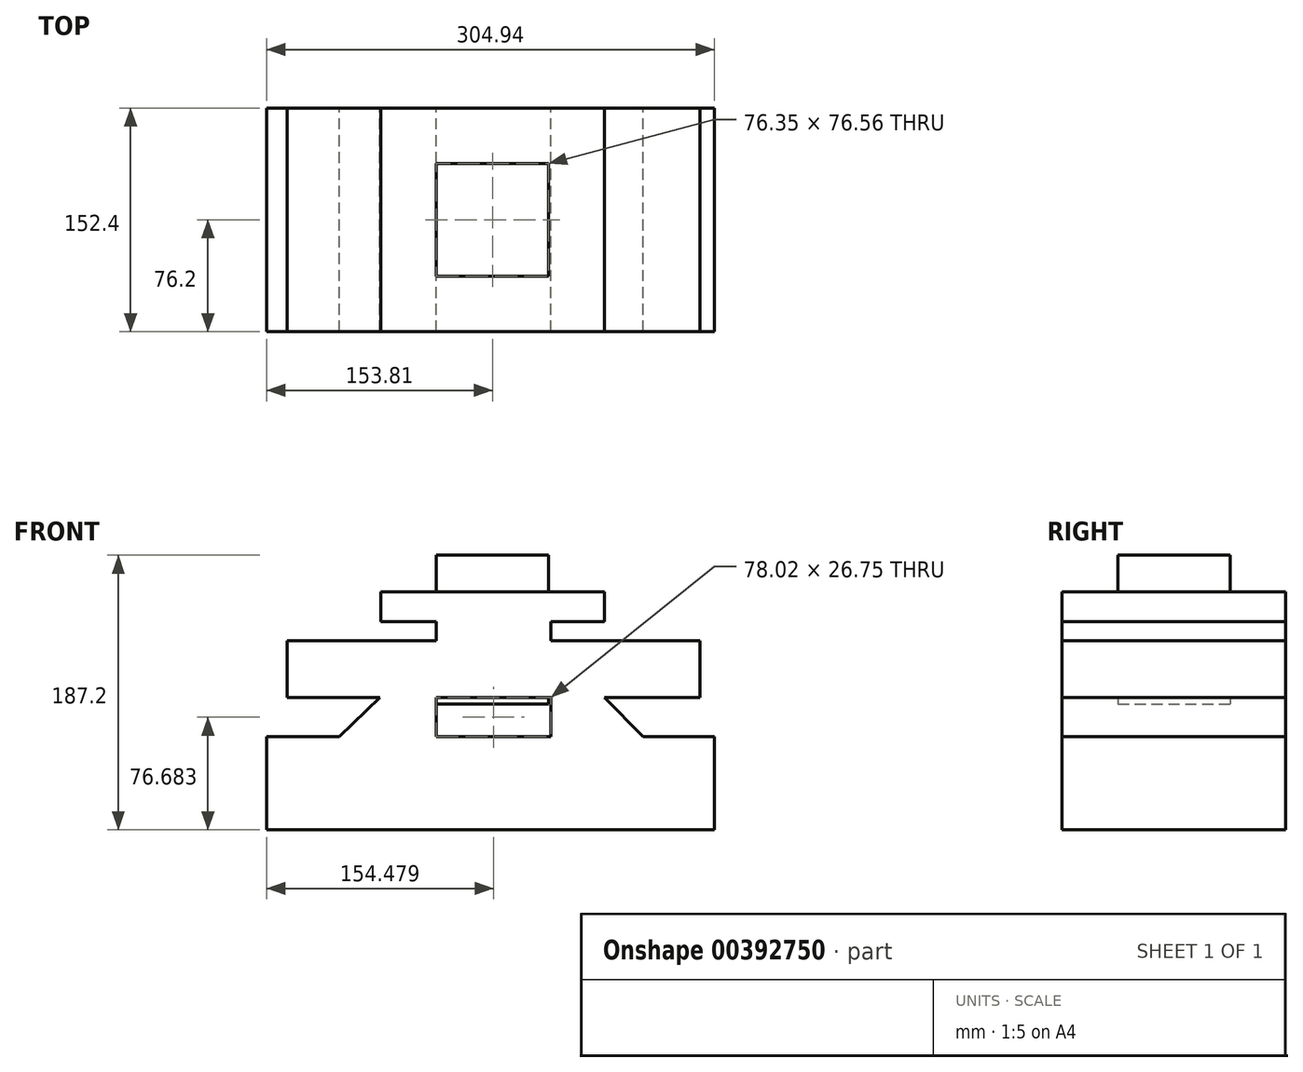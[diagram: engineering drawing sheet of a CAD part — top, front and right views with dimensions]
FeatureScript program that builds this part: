
annotation { "Feature Type Name" : "Feature", "Feature Type Description" : "" }
export const myFeature = defineFeature(function(context is Context, id is Id, definition is map)
    precondition{}
    {
        {
            var Q0;
            Q0=qCreatedBy(makeId("Front.planeOp"),FACE);
            var sketch = newSketch(context, id + "F0", { "sketchPlane" : qUnion([Q0])});
            skLineSegment(sketch, "E0", {"start": v(-153.8, -85.6) * mm, "end": v(151.13, -85.6) * mm});
            skLineSegment(sketch, "E1", {"start": v(151.13, -85.6) * mm, "end": v(151.13, -22.3) * mm});
            skLineSegment(sketch, "E2", {"start": v(-153.8, -85.6) * mm, "end": v(-153.8, -22.3) * mm});
            skLineSegment(sketch, "E3", {"start": v(-153.8, -22.3) * mm, "end": v(151.13, -22.3) * mm});
            skLineSegment(sketch, "E4", {"start": v(-38.34, -22.3) * mm, "end": v(-38.34, 4.46) * mm});
            skLineSegment(sketch, "E5", {"start": v(-38.34, 4.46) * mm, "end": v(39.68, 4.46) * mm});
            skLineSegment(sketch, "E6", {"start": v(39.68, 4.46) * mm, "end": v(39.68, -22.3) * mm});
            skLineSegment(sketch, "E7", {"start": v(-38.34, 4.46) * mm, "end": v(-139.99, 4.46) * mm});
            skLineSegment(sketch, "E8", {"start": v(39.68, 4.46) * mm, "end": v(141.33, 4.46) * mm});
            skLineSegment(sketch, "E9", {"start": v(-139.99, 4.46) * mm, "end": v(-139.99, 43.24) * mm});
            skLineSegment(sketch, "E10", {"start": v(-139.99, 43.24) * mm, "end": v(141.33, 43.24) * mm});
            skLineSegment(sketch, "E11", {"start": v(141.33, 43.24) * mm, "end": v(141.33, 4.46) * mm});
            skLineSegment(sketch, "E12", {"start": v(-76.68, 43.24) * mm, "end": v(-76.68, 4.46) * mm});
            skLineSegment(sketch, "E13", {"start": v(0, 4.46) * mm, "end": v(0, 43.24) * mm});
            skLineSegment(sketch, "E14", {"start": v(76.24, 43.24) * mm, "end": v(76.24, 4.46) * mm});
            skLineSegment(sketch, "E15", {"start": v(-38.34, 43.24) * mm, "end": v(-38.34, 56.17) * mm});
            skLineSegment(sketch, "E16", {"start": v(39.68, 56.17) * mm, "end": v(-38.34, 56.17) * mm});
            skLineSegment(sketch, "E17", {"start": v(39.68, 56.17) * mm, "end": v(39.68, 43.24) * mm});
            skLineSegment(sketch, "E18", {"start": v(-38.34, 56.17) * mm, "end": v(-76.24, 56.17) * mm});
            skLineSegment(sketch, "E19", {"start": v(-76.24, 56.17) * mm, "end": v(-76.24, 76.68) * mm});
            skLineSegment(sketch, "E20", {"start": v(-76.24, 76.68) * mm, "end": v(76.24, 76.68) * mm});
            skLineSegment(sketch, "E21", {"start": v(39.68, 56.17) * mm, "end": v(76.24, 56.17) * mm});
            skLineSegment(sketch, "E22", {"start": v(76.24, 56.17) * mm, "end": v(76.24, 76.68) * mm});
            skLineSegment(sketch, "E23", {"start": v(-76.68, 4.46) * mm, "end": v(-104.32, -22.3) * mm});
            skLineSegment(sketch, "E24", {"start": v(76.24, 4.46) * mm, "end": v(102.54, -22.3) * mm});
            skSolve(sketch);
        }
        {
            var Q0;
            Q0 = qSketchRegion(id + "F0", true);
            extrude(context, id + "F1", {"entities" : qUnion([Q0]), "endBound" : BoundingType.SYMMETRIC, "depth" : 152.4 * mm});
        }
        {
            var Q0;
            Q0=qCreatedBy(makeId("Top.planeOp"),FACE);
            var sketch = newSketch(context, id + "F2", { "sketchPlane" : qUnion([Q0])});
            skLineSegment(sketch, "E25.bottom", {"start": v(-38.18, -38.28) * mm, "end": v(38.18, -38.28) * mm});
            skLineSegment(sketch, "E25.top", {"start": v(-38.18, 38.28) * mm, "end": v(38.18, 38.28) * mm});
            skLineSegment(sketch, "E25.left", {"start": v(-38.18, -38.28) * mm, "end": v(-38.18, 38.28) * mm});
            skLineSegment(sketch, "E25.right", {"start": v(38.18, -38.28) * mm, "end": v(38.18, 38.28) * mm});
            skPoint(sketch, "E25.middle", {"position": v(0, 0) * mm});
            skSolve(sketch);
        }
        {
            var Q0;
            Q0 = qSketchRegion(id + "F2", true);
            extrude(context, id + "F3", {"entities" : qUnion([Q0]), "operationType" : NewBodyOperationType.ADD, "depth" : 101.6 * mm});
        }
    });
